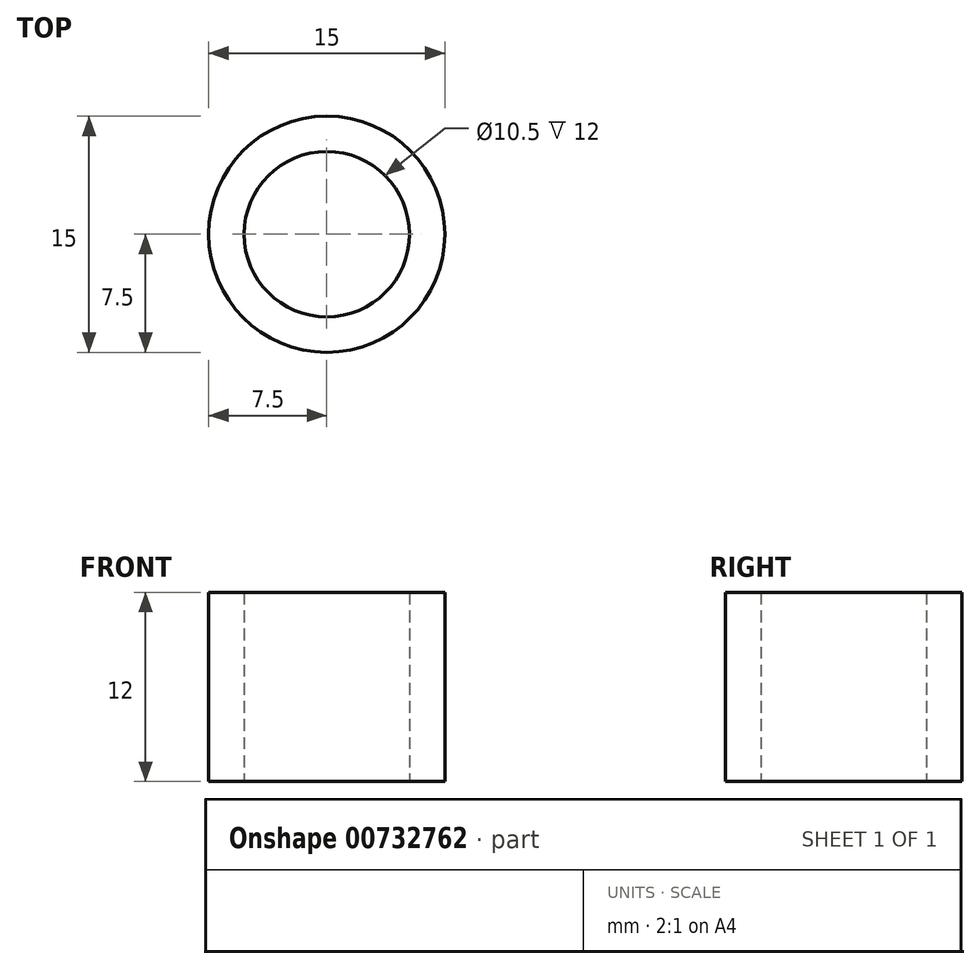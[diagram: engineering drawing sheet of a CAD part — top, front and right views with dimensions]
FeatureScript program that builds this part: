
annotation { "Feature Type Name" : "Feature", "Feature Type Description" : "" }
export const myFeature = defineFeature(function(context is Context, id is Id, definition is map)
    precondition{}
    {
        {
            var Q0;
            Q0=qCreatedBy(makeId("Top.planeOp"),FACE);
            var sketch = newSketch(context, id + "F0", { "sketchPlane" : qUnion([Q0])});
            skCircle(sketch, "E0", {"center": v(0, 0) * mm, "radius": 5.25 * mm});
            skCircle(sketch, "E1", {"center": v(0, 0) * mm, "radius": 7.5 * mm});
            skSolve(sketch);
        }
        {
            var Q0;
            Q0 = qSketchRegion(id + "F0", true);
            extrude(context, id + "F1", {"entities" : qUnion([Q0]), "endBound" : BoundingType.SYMMETRIC, "depth" : 12 * mm, "offsetDistance" : 25 * mm});
        }
    });
